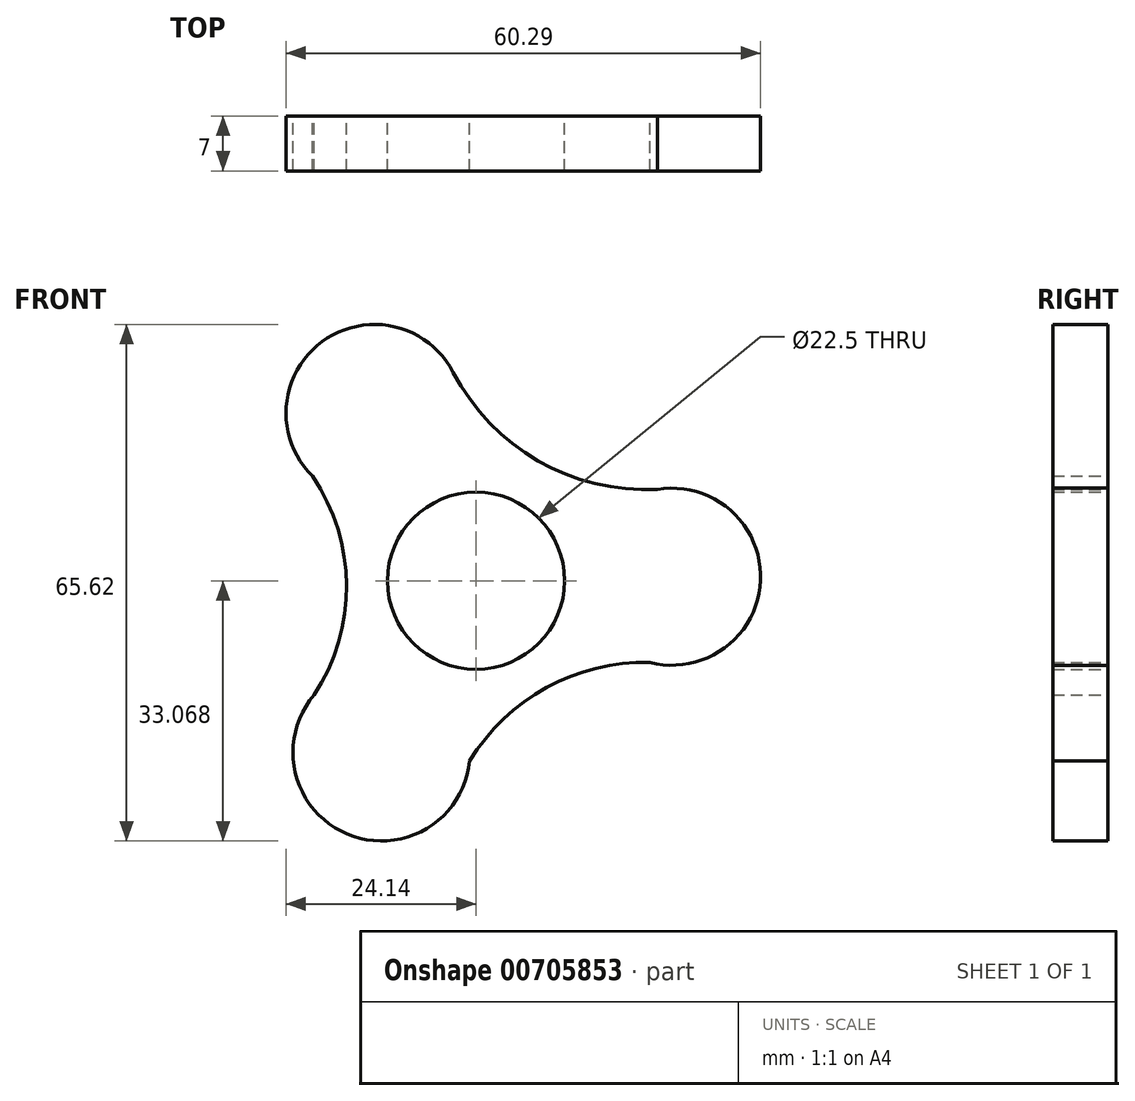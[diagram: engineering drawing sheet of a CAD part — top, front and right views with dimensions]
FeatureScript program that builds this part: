
annotation { "Feature Type Name" : "Feature", "Feature Type Description" : "" }
export const myFeature = defineFeature(function(context is Context, id is Id, definition is map)
    precondition{}
    {
        {
            var Q0;
            Q0=qCreatedBy(makeId("Front.planeOp"),FACE);
            var sketch = newSketch(context, id + "F0", { "sketchPlane" : qUnion([Q0])});
            skCircle(sketch, "E0", {"center": v(0, 29.1) * mm, "radius": 11.25 * mm});
            skCircle(sketch, "E1.1.0", {"center": v(0.88, -14.02) * mm, "radius": 11.25 * mm});
            skCircle(sketch, "E1.2.0", {"center": v(37.79, 8.3) * mm, "radius": 11.25 * mm});
            skPoint(sketch, "E1.center", {"position": v(12.9, 7.8) * mm});
            skCircle(sketch, "E2", {"center": v(12.9, 7.8) * mm, "radius": 11.25 * mm});
            skLineSegment(sketch, "E3", {"start": v(0, 29.1) * mm, "end": v(0, 49.34) * mm});
            skLineSegment(sketch, "E4", {"start": v(0, 49.34) * mm, "end": v(0, 29.1) * mm});
            skLineSegment(sketch, "E5", {"start": v(37.79, 8.3) * mm, "end": v(37.79, 8.3) * mm});
            skPoint(sketch, "E6.orphan", {"position": v(-58.53, -47.05) * mm});
            skPoint(sketch, "E7.orphan", {"position": v(-19.5, -47.05) * mm});
            skPoint(sketch, "E8.end.orphan", {"position": v(58.53, -47.05) * mm});
            skPoint(sketch, "E9.orphan", {"position": v(0, 15.86) * mm});
            skArc(sketch, "E10", {"start": v(10, 34.27) * mm, "mid": v(21.6, 22.58) * mm, "end": v(37.79, 19.56) * mm});
            skArc(sketch, "E11", {"start": v(34.97, -2.58) * mm, "mid": v(21.86, -5.79) * mm, "end": v(12.08, -15.1) * mm});
            skArc(sketch, "E12", {"start": v(-7.68, -6.73) * mm, "mid": v(-3.61, 8.72) * mm, "end": v(-9.74, 23.48) * mm});
            skPoint(sketch, "E13.orphan", {"position": v(-22.94, 15.86) * mm});
            skPoint(sketch, "E14.end.orphan", {"position": v(22.94, 15.86) * mm});
            skPoint(sketch, "E15.orphan", {"position": v(52.18, 0) * mm});
            skPoint(sketch, "E16.start.orphan", {"position": v(-5.96, 19.56) * mm});
            skSolve(sketch);
        }
        {
            var Q0;
            Q0 = qSketchRegion(id + "F0", true);
            extrude(context, id + "F1", {"entities" : qUnion([Q0]), "depth" : 7 * mm, "offsetDistance" : 25 * mm});
        }
    });
